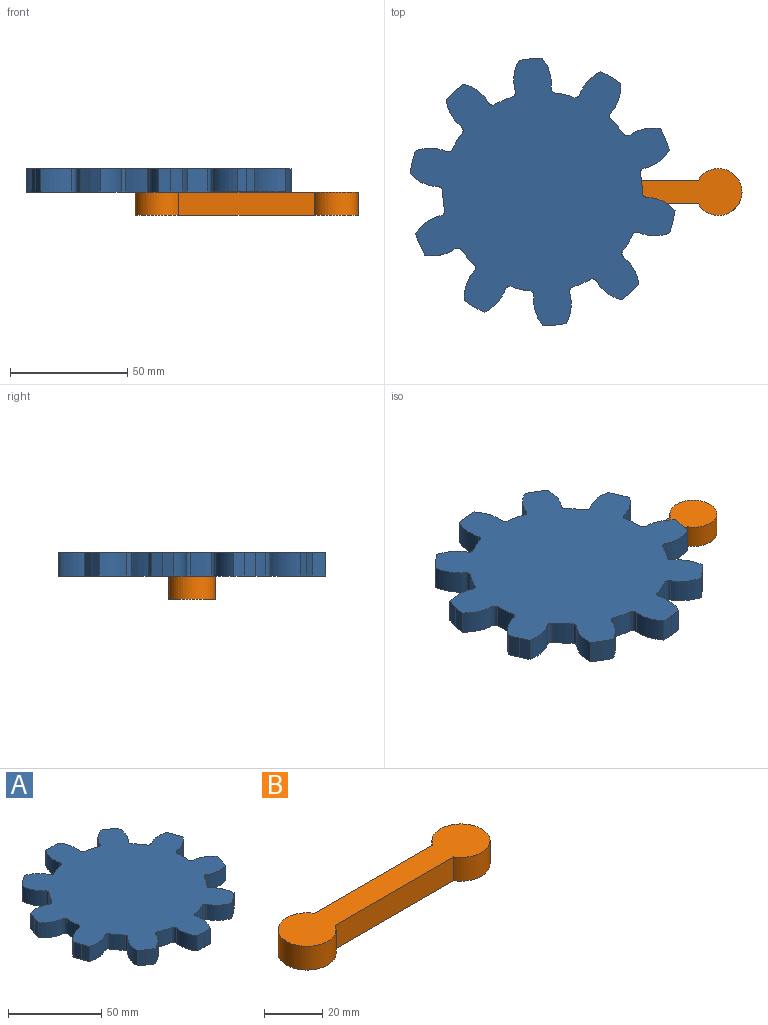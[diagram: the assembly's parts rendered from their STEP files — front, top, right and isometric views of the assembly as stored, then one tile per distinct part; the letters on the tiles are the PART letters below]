
ASSEMBLY  parts=2 mates=1
PART A: 72 faces, bbox 111.4x114x10 mm
  f0: cylinder r=2mm len=10mm, axis (0,0,-1), area 24.6mm2, adj f8,f15,f16,f17
  f1: cylinder r=42.5mm len=10mm, axis (0,0,-1), area 92.4mm2, adj f16,f17,f23,f67
  f2: cylinder r=42.5mm len=10mm, axis (0,0,-1), area 92.4mm2, adj f16,f17,f22,f29
  f3: cylinder r=42.5mm len=10mm, axis (0,0,-1), area 92.4mm2, adj f16,f17,f28,f35
  f4: cylinder r=42.5mm len=10mm, axis (0,0,-1), area 92.4mm2, adj f16,f17,f34,f41
  f5: cylinder r=42.5mm len=10mm, axis (0,0,-1), area 92.4mm2, adj f16,f17,f40,f47
  f6: cylinder r=42.5mm len=10mm, axis (0,0,-1), area 92.4mm2, adj f16,f17,f46,f53
  f7: cylinder r=42.5mm len=10mm, axis (0,0,-1), area 92.4mm2, adj f16,f17,f52,f59
  f8: cylinder r=42.5mm len=10mm, axis (0,0,-1), area 92.4mm2, adj f0,f16,f17,f58
  f9: cylinder r=42.5mm len=10mm, axis (0,0,-1), area 92.4mm2, adj f11,f16,f17,f65
  f10: cylinder r=42.5mm len=10mm, axis (0,0,-1), area 92.4mm2, adj f16,f17,f64,f66
  f11: cylinder r=2mm len=10mm, axis (0,0,-1), area 24.6mm2, adj f9,f12,f16,f17
  f12: cylinder r=17.45mm len=13.04mm, axis (0,0,-1), area 137.2mm2, adj f11,f13,f16,f17
  f13: plane 10x4.93mm, normal (0.03,1,0), area 49.4mm2, adj f12,f14,f16,f17
  f14: plane 10x4.93mm, normal (-0.06,1,0), area 49.4mm2, adj f13,f15,f16,f17
  f15: cylinder r=17.45mm len=13.12mm, axis (0,0,-1), area 137.2mm2, adj f0,f14,f16,f17
  f16: plane 113.99x111.42mm, normal (0,0,1), area 7805.6mm2, adj f0,f1,f2,f3,f4,f5,f6,f7
  f17: plane 113.99x111.42mm, normal (0,0,-1), area 7805.6mm2, adj f0,f1,f2,f3,f4,f5,f6,f7
  f18: cylinder r=17.45mm len=13.32mm, axis (0,0,-1), area 137.2mm2, adj f16,f17,f19,f22
  f19: plane 10x4.65mm, normal (0.94,-0.34,0), area 49.4mm2, adj f16,f17,f18,f20
  f20: plane 10x4.78mm, normal (0.97,-0.25,0), area 49.4mm2, adj f16,f17,f19,f21
  f21: cylinder r=17.45mm len=11.68mm, axis (0,0,-1), area 137.2mm2, adj f16,f17,f20,f23
  f22: cylinder r=2mm len=10mm, axis (0,0,-1), area 24.6mm2, adj f2,f16,f17,f18
  f23: cylinder r=2mm len=10mm, axis (0,0,-1), area 24.6mm2, adj f1,f16,f17,f21
  f24: cylinder r=17.45mm len=10.06mm, axis (0,0,-1), area 137.2mm2, adj f16,f17,f25,f28
  f25: plane 10x4.08mm, normal (0.56,-0.83,0), area 49.4mm2, adj f16,f17,f24,f26
  f26: plane 10x3.82mm, normal (0.63,-0.77,0), area 49.4mm2, adj f16,f17,f25,f27
  f27: cylinder r=17.45mm len=12.13mm, axis (0,0,-1), area 137.2mm2, adj f16,f17,f26,f29
  f28: cylinder r=2mm len=10mm, axis (0,0,-1), area 24.6mm2, adj f3,f16,f17,f24
  f29: cylinder r=2mm len=10mm, axis (0,0,-1), area 24.6mm2, adj f2,f16,f17,f27
  f30: cylinder r=17.45mm len=13.04mm, axis (0,0,-1), area 137.2mm2, adj f16,f17,f31,f34
  f31: plane 10x4.93mm, normal (-0.03,-1,0), area 49.4mm2, adj f16,f17,f30,f32
  f32: plane 10x4.93mm, normal (0.06,-1,0), area 49.4mm2, adj f16,f17,f31,f33
  f33: cylinder r=17.45mm len=13.12mm, axis (0,0,-1), area 137.2mm2, adj f16,f17,f32,f35
  f34: cylinder r=2mm len=10mm, axis (0,0,-1), area 24.6mm2, adj f4,f16,f17,f30
  f35: cylinder r=2mm len=10mm, axis (0,0,-1), area 24.6mm2, adj f3,f16,f17,f33
  f36: cylinder r=17.45mm len=12.29mm, axis (0,0,-1), area 137.2mm2, adj f16,f17,f37,f40
  f37: plane 10x3.91mm, normal (-0.61,-0.79,0), area 49.4mm2, adj f16,f17,f36,f38
  f38: plane 10x4.15mm, normal (-0.54,-0.84,0), area 49.4mm2, adj f16,f17,f37,f39
  f39: cylinder r=17.45mm len=10mm, axis (0,0,-1), area 137.2mm2, adj f16,f17,f38,f41
  f40: cylinder r=2mm len=10mm, axis (0,0,-1), area 24.6mm2, adj f5,f16,f17,f36
  f41: cylinder r=2mm len=10mm, axis (0,0,-1), area 24.6mm2, adj f4,f16,f17,f39
  f42: cylinder r=17.45mm len=11.49mm, axis (0,0,-1), area 137.2mm2, adj f16,f17,f43,f46
  f43: plane 10x4.74mm, normal (-0.96,-0.28,0), area 49.4mm2, adj f16,f17,f42,f44
  f44: plane 10x4.6mm, normal (-0.93,-0.36,0), area 49.4mm2, adj f16,f17,f43,f45
  f45: cylinder r=17.45mm len=13.28mm, axis (0,0,-1), area 137.2mm2, adj f16,f17,f44,f47
  f46: cylinder r=2mm len=10mm, axis (0,0,-1), area 24.6mm2, adj f6,f16,f17,f42
  f47: cylinder r=2mm len=10mm, axis (0,0,-1), area 24.6mm2, adj f5,f16,f17,f45
  f48: cylinder r=17.45mm len=13.32mm, axis (0,0,-1), area 137.2mm2, adj f16,f17,f49,f52
  f49: plane 10x4.65mm, normal (-0.94,0.34,0), area 49.4mm2, adj f16,f17,f48,f50
  f50: plane 10x4.78mm, normal (-0.97,0.25,0), area 49.4mm2, adj f16,f17,f49,f51
  f51: cylinder r=17.45mm len=11.68mm, axis (0,0,-1), area 137.2mm2, adj f16,f17,f50,f53
  f52: cylinder r=2mm len=10mm, axis (0,0,-1), area 24.6mm2, adj f7,f16,f17,f48
  f53: cylinder r=2mm len=10mm, axis (0,0,-1), area 24.6mm2, adj f6,f16,f17,f51
  f54: cylinder r=17.45mm len=10.06mm, axis (0,0,-1), area 137.2mm2, adj f16,f17,f55,f58
  f55: plane 10x4.08mm, normal (-0.56,0.83,0), area 49.4mm2, adj f16,f17,f54,f56
  f56: plane 10x3.82mm, normal (-0.63,0.77,0), area 49.4mm2, adj f16,f17,f55,f57
  f57: cylinder r=17.45mm len=12.13mm, axis (0,0,-1), area 137.2mm2, adj f16,f17,f56,f59
  f58: cylinder r=2mm len=10mm, axis (0,0,-1), area 24.6mm2, adj f8,f16,f17,f54
  f59: cylinder r=2mm len=10mm, axis (0,0,-1), area 24.6mm2, adj f7,f16,f17,f57
  f60: cylinder r=17.45mm len=12.29mm, axis (0,0,-1), area 137.2mm2, adj f16,f17,f61,f64
  f61: plane 10x3.91mm, normal (0.61,0.79,0), area 49.4mm2, adj f16,f17,f60,f62
  f62: plane 10x4.15mm, normal (0.54,0.84,0), area 49.4mm2, adj f16,f17,f61,f63
  f63: cylinder r=17.45mm len=10mm, axis (0,0,-1), area 137.2mm2, adj f16,f17,f62,f65
  f64: cylinder r=2mm len=10mm, axis (0,0,-1), area 24.6mm2, adj f10,f16,f17,f60
  f65: cylinder r=2mm len=10mm, axis (0,0,-1), area 24.6mm2, adj f9,f16,f17,f63
  f66: cylinder r=2mm len=10mm, axis (0,0,-1), area 24.6mm2, adj f10,f16,f17,f71
  f67: cylinder r=2mm len=10mm, axis (0,0,-1), area 24.6mm2, adj f1,f16,f17,f68
  f68: cylinder r=17.45mm len=11.49mm, axis (0,0,-1), area 137.2mm2, adj f16,f17,f67,f69
  f69: plane 10x4.74mm, normal (0.96,0.28,0), area 49.4mm2, adj f16,f17,f68,f70
  f70: plane 10x4.6mm, normal (0.93,0.36,0), area 49.4mm2, adj f16,f17,f69,f71
  f71: cylinder r=17.45mm len=13.28mm, axis (0,0,-1), area 137.2mm2, adj f16,f17,f66,f70
PART B: 6 faces, bbox 95x20x10 mm
  f0: plane 57.68x10mm, normal (0,1,0), area 576.8mm2, adj f1,f3,f4,f5
  f1: cylinder r=10mm len=20mm, axis (0,0,-1), area 523.6mm2, adj f0,f2,f4,f5
  f2: plane 57.68x10mm, normal (0,-1,0), area 576.8mm2, adj f1,f3,f4,f5
  f3: cylinder r=10mm len=20mm, axis (0,0,-1), area 523.6mm2, adj f0,f2,f4,f5
  f4: plane 95x20mm, normal (0,0,1), area 1187mm2, adj f0,f1,f2,f3
  f5: plane 95x20mm, normal (0,0,-1), area 1187mm2, adj f0,f1,f2,f3
PLACE A rot(axis=(0,0,-1),31.7deg) t=(0,0,0)mm
PLACE B t=(0,0,-10)mm
MATE revolute B.f1 <-> A.f1  axis (0,0,1) through (0,0,0)mm
